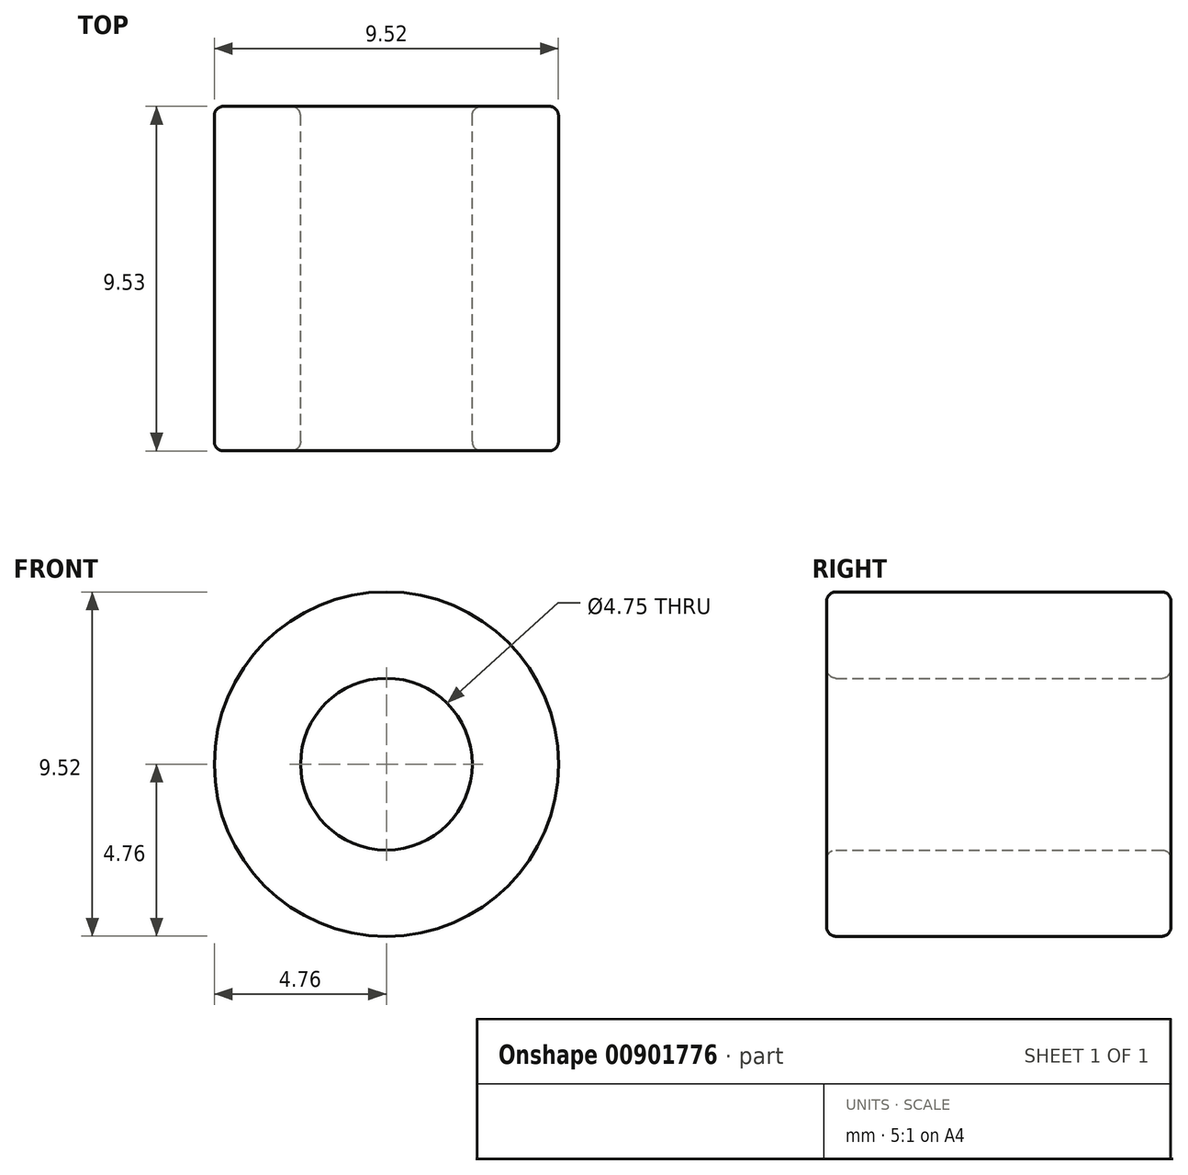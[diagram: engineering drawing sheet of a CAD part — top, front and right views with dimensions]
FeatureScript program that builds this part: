
annotation { "Feature Type Name" : "Feature", "Feature Type Description" : "" }
export const myFeature = defineFeature(function(context is Context, id is Id, definition is map)
    precondition{}
    {
        {
            var Q0;
            Q0=qCreatedBy(makeId("Front.planeOp"),FACE);
            var sketch = newSketch(context, id + "F0", { "sketchPlane" : qUnion([Q0])});
            skCircle(sketch, "E0", {"center": v(0, 0) * mm, "radius": 2.37 * mm});
            skCircle(sketch, "E1", {"center": v(0, 0) * mm, "radius": 4.76 * mm});
            skSolve(sketch);
        }
        {
            var Q0;
            Q0=makeQuery(id+"F0.imprint","IMPRINT",FACE,{"disambiguationData":[TD([[makeQuery(id+"F0.imprint","IMPRINT",EDGE,{"derivedFrom":sQuery(id+"F0.wireOp",EDGE,"E0")}),-1.0]])]});
            extrude(context, id + "F1", {"entities" : qUnion([Q0]), "depth" : 9.52 * mm, "offsetDistance" : 25.4 * mm});
        }
        {
            var Q0;
            Q0=makeQuery(id+"F1.opExtrude","CAP_EDGE",EDGE,{"disambiguationData":[OSD([sQuery(id+"F0.wireOp",EDGE,"E1")])],"isStart":false});
            var Q1;
            Q1=makeQuery(id+"F1.opExtrude","CAP_EDGE",EDGE,{"disambiguationData":[OSD([sQuery(id+"F0.wireOp",EDGE,"E1")])],"isStart":true});
            fillet(context, id + "F2", {"entities" : qUnion([Q0, Q1]), "radius" : 0.25 * mm, "tangentPropagation" : true, "allowEdgeOverflow" : false});
        }
        {
            var Q0;
            Q0=makeQuery(id+"F1.opExtrude","CAP_EDGE",EDGE,{"disambiguationData":[OSD([sQuery(id+"F0.wireOp",EDGE,"E0")])],"isStart":false});
            var Q1;
            Q1=makeQuery(id+"F1.opExtrude","CAP_EDGE",EDGE,{"disambiguationData":[OSD([sQuery(id+"F0.wireOp",EDGE,"E0")])],"isStart":true});
            fillet(context, id + "F3", {"entities" : qUnion([Q0, Q1]), "radius" : 0.25 * mm, "tangentPropagation" : true, "allowEdgeOverflow" : false});
        }
    });
